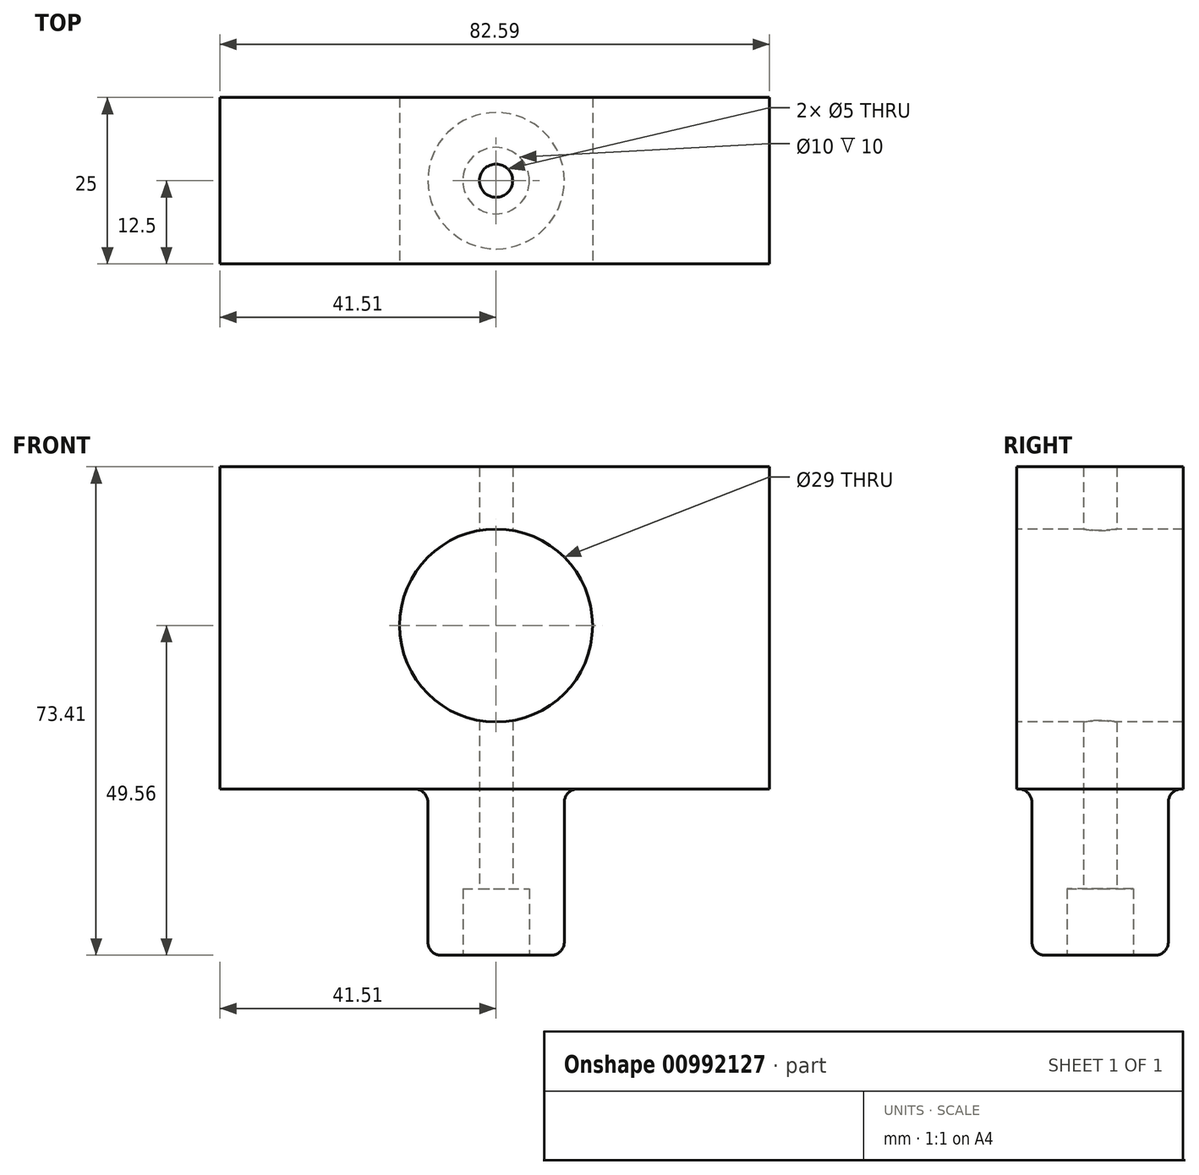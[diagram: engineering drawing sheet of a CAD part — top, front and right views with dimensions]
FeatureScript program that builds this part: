
annotation { "Feature Type Name" : "Feature", "Feature Type Description" : "" }
export const myFeature = defineFeature(function(context is Context, id is Id, definition is map)
    precondition{}
    {
        {
            var Q0;
            Q0=qCreatedBy(makeId("Front.planeOp"),FACE);
            var sketch = newSketch(context, id + "F0", { "sketchPlane" : qUnion([Q0])});
            skLineSegment(sketch, "E0.bottom", {"start": v(-41.51, 23.85) * mm, "end": v(41.08, 23.85) * mm});
            skLineSegment(sketch, "E0.top", {"start": v(-41.51, -24.56) * mm, "end": v(41.08, -24.56) * mm});
            skLineSegment(sketch, "E0.left", {"start": v(-41.51, 23.85) * mm, "end": v(-41.51, -24.56) * mm});
            skLineSegment(sketch, "E0.right", {"start": v(41.08, 23.85) * mm, "end": v(41.08, -24.56) * mm});
            skSolve(sketch);
        }
        {
            var Q0;
            Q0 = qSketchRegion(id + "F0", true);
            extrude(context, id + "F1", {"entities" : qUnion([Q0]), "endBound" : BoundingType.SYMMETRIC, "depth" : 25 * mm, "offsetDistance" : 25 * mm});
        }
        {
            var Q0;
            Q0=makeQuery(id+"F1.opExtrude","CAP_FACE",FACE,{"disambiguationData":[OSD([sQuery(id+"F0.wireOp",EDGE,"E0.bottom"),sQuery(id+"F0.wireOp",EDGE,"E0.top"),sQuery(id+"F0.wireOp",EDGE,"E0.left"),sQuery(id+"F0.wireOp",EDGE,"E0.right")])],"isStart":false});
            var sketch = newSketch(context, id + "F2", { "sketchPlane" : qUnion([Q0])});
            skCircle(sketch, "E1", {"center": v(0, 0) * mm, "radius": 14.5 * mm});
            skSolve(sketch);
        }
        {
            var Q0;
            Q0 = qSketchRegion(id + "F2", true);
            extrude(context, id + "F3", {"entities" : qUnion([Q0]), "operationType" : NewBodyOperationType.REMOVE, "endBound" : BoundingType.THROUGH_ALL, "oppositeDirection" : true, "depth" : 25 * mm, "offsetDistance" : 25 * mm});
        }
        {
            var Q0;
            Q0=makeQuery(id+"F1.opExtrude","SWEPT_FACE",FACE,{"disambiguationData":[OSD([sQuery(id+"F0.wireOp",EDGE,"E0.top")])]});
            var sketch = newSketch(context, id + "F4", { "sketchPlane" : qUnion([Q0])});
            skCircle(sketch, "E2", {"center": v(0, 0) * mm, "radius": 10.25 * mm});
            skSolve(sketch);
        }
        {
            var Q0;
            Q0 = qSketchRegion(id + "F4", true);
            extrude(context, id + "F5", {"entities" : qUnion([Q0]), "operationType" : NewBodyOperationType.ADD, "depth" : 25 * mm, "offsetDistance" : 25 * mm});
        }
        {
            var Q0;
            Q0=makeQuery(id+"F5.opExtrude","CAP_FACE",FACE,{"disambiguationData":[OSD([sQuery(id+"F4.wireOp",EDGE,"E2")])],"isStart":false});
            var Q1;
            Q1=makeQuery(id+"F5.opExtrude","SWEPT_FACE",FACE,{"disambiguationData":[OSD([sQuery(id+"F4.wireOp",EDGE,"E2")])]});
            fillet(context, id + "F6", {"entities" : qUnion([Q0, Q1]), "radius" : 2 * mm, "tangentPropagation" : true, "allowEdgeOverflow" : false});
        }
        {
            var Q0;
            Q0=makeQuery(id+"F5.opExtrude","CAP_FACE",FACE,{"disambiguationData":[OSD([sQuery(id+"F4.wireOp",EDGE,"E2")])],"isStart":false});
            var sketch = newSketch(context, id + "F7", { "sketchPlane" : qUnion([Q0])});
            skPoint(sketch, "E3", {"position": v(0, 0) * mm});
            skSolve(sketch);
        }
        {
            var Q0;
            Q0=sQuery(id+"F7.wireOp",VERTEX,"E3");
            var Q1;
            Q1=makeQuery(id+"F1.opExtrude","SWEPT_BODY",BODY,{"disambiguationData":[OSD([sQuery(id+"F0.wireOp",EDGE,"E0.bottom"),sQuery(id+"F0.wireOp",EDGE,"E0.top"),sQuery(id+"F0.wireOp",EDGE,"E0.left"),sQuery(id+"F0.wireOp",EDGE,"E0.right")])]});
            hole(context, id + "F8", {"style" : HoleStyle.C_BORE, "endStyle" : HoleEndStyle.THROUGH, "holeDiameter" : 5 * mm, "cBoreDiameter" : 10 * mm, "cBoreDepth" : 10 * mm, "majorDiameter" : 5 * mm, "isTappedThrough" : true, "tappedDepth" : 12 * mm, "tapClearance" : 3, "startFromSketch" : true, "locations" : qUnion([Q0]), "scope" : qUnion([Q1])});
        }
    });
